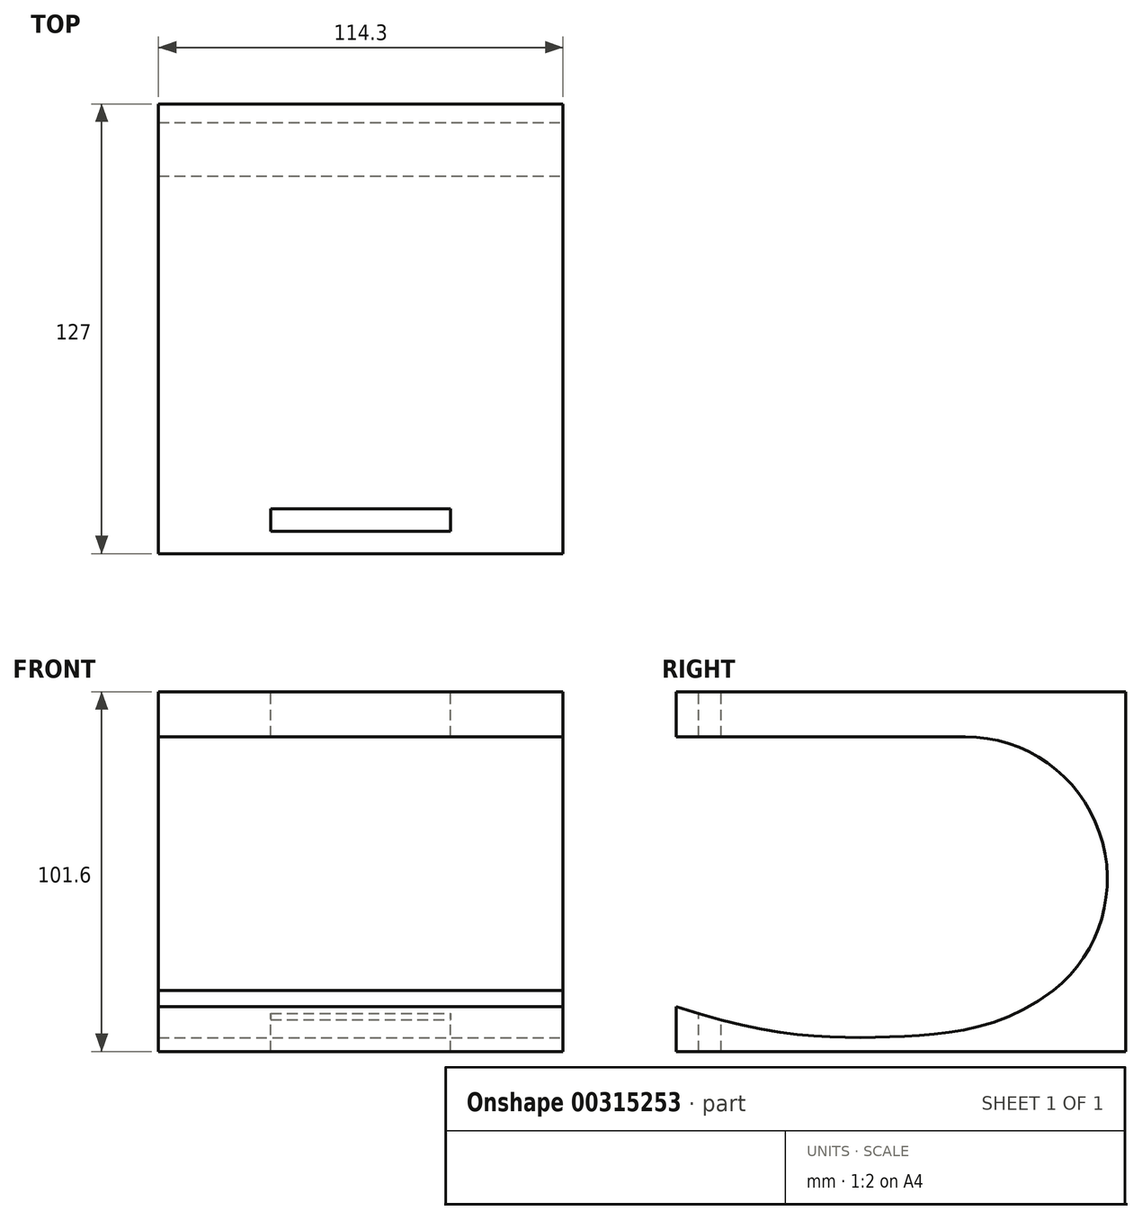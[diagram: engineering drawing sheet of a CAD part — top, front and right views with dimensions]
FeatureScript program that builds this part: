
annotation { "Feature Type Name" : "Feature", "Feature Type Description" : "" }
export const myFeature = defineFeature(function(context is Context, id is Id, definition is map)
    precondition{}
    {
        {
            var Q0;
            Q0=qCreatedBy(makeId("Front.planeOp"),FACE);
            var sketch = newSketch(context, id + "F0", { "sketchPlane" : qUnion([Q0])});
            skLineSegment(sketch, "E0.bottom", {"start": v(-39.44, 63.4) * mm, "end": v(74.86, 63.4) * mm});
            skLineSegment(sketch, "E0.top", {"start": v(-39.44, -38.2) * mm, "end": v(74.86, -38.2) * mm});
            skLineSegment(sketch, "E0.left", {"start": v(-39.44, 63.4) * mm, "end": v(-39.44, -38.2) * mm});
            skLineSegment(sketch, "E0.right", {"start": v(74.86, 63.4) * mm, "end": v(74.86, -38.2) * mm});
            skSolve(sketch);
        }
        {
            var Q0;
            Q0 = qSketchRegion(id + "F0", true);
            extrude(context, id + "F1", {"entities" : qUnion([Q0]), "depth" : 127 * mm});
        }
        {
            var Q0;
            Q0=qCreatedBy(makeId("Right.planeOp"),FACE);
            var sketch = newSketch(context, id + "F2", { "sketchPlane" : qUnion([Q0])});
            skFitSpline(sketch, "E1", {"points": [v(-127, -25.5) * mm, v(-65.32, -34) * mm, v(-20.44, -20.97) * mm], "startDerivative": vector(157, -52.04) * mm, "endDerivative": vector(96.83, 73.78) * mm});
            skLineSegment(sketch, "E2", {"start": v(-127, 50.7) * mm, "end": v(-45.4, 50.7) * mm});
            skArc(sketch, "E3", {"start": v(-45.4, 50.7) * mm, "mid": v(-7.46, 23.74) * mm, "end": v(-20.44, -20.97) * mm});
            skLineSegment(sketch, "E4", {"start": v(-127, 50.7) * mm, "end": v(-127, -25.5) * mm});
            skSolve(sketch);
        }
        {
            var Q0;
            Q0 = qSketchRegion(id + "F2", true);
            extrude(context, id + "F3", {"entities" : qUnion([Q0]), "operationType" : NewBodyOperationType.REMOVE, "endBound" : BoundingType.THROUGH_ALL, "oppositeDirection" : true, "depth" : 25.4 * mm, "hasSecondDirection" : true, "secondDirectionBound" : SecondDirectionBoundingType.THROUGH_ALL, "secondDirectionOppositeDirection" : false, "secondDirectionDepth" : 25.4 * mm});
        }
        {
            var Q0;
            Q0=qCreatedBy(makeId("Top.planeOp"),FACE);
            var sketch = newSketch(context, id + "F4", { "sketchPlane" : qUnion([Q0])});
            skLineSegment(sketch, "E5.bottom", {"start": v(-19.6, -179.52) * mm, "end": v(59.34, -179.52) * mm});
            skLineSegment(sketch, "E5.top", {"start": v(-19.6, -189.23) * mm, "end": v(59.34, -189.23) * mm});
            skLineSegment(sketch, "E5.left", {"start": v(-19.6, -179.52) * mm, "end": v(-19.6, -189.23) * mm});
            skLineSegment(sketch, "E5.right", {"start": v(59.34, -179.52) * mm, "end": v(59.34, -189.23) * mm});
            skLineSegment(sketch, "E6", {"start": v(17.71, 15.75) * mm, "end": v(17.71, -136.65) * mm, "construction": true});
            skLineSegment(sketch, "E7", {"start": v(-7.69, -114.3) * mm, "end": v(17.71, -114.3) * mm});
            skLineSegment(sketch, "E8", {"start": v(17.71, -120.65) * mm, "end": v(-7.69, -120.65) * mm});
            skLineSegment(sketch, "E9", {"start": v(-7.69, -120.65) * mm, "end": v(-7.69, -114.3) * mm});
            skLineSegment(sketch, "E10.MirrorCS", {"start": v(17.71, -120.65) * mm, "end": v(43.11, -120.65) * mm});
            skLineSegment(sketch, "E11.MirrorCS", {"start": v(43.11, -114.3) * mm, "end": v(17.71, -114.3) * mm});
            skLineSegment(sketch, "E12.MirrorCS", {"start": v(43.11, -120.65) * mm, "end": v(43.11, -114.3) * mm});
            skSolve(sketch);
        }
        {
            var Q0;
            Q0 = qSketchRegion(id + "F4", true);
            extrude(context, id + "F5", {"entities" : qUnion([Q0]), "operationType" : NewBodyOperationType.REMOVE, "endBound" : BoundingType.THROUGH_ALL, "oppositeDirection" : true, "depth" : 25.4 * mm, "hasSecondDirection" : true, "secondDirectionBound" : SecondDirectionBoundingType.THROUGH_ALL, "secondDirectionOppositeDirection" : false, "secondDirectionDepth" : 25.4 * mm});
        }
    });
